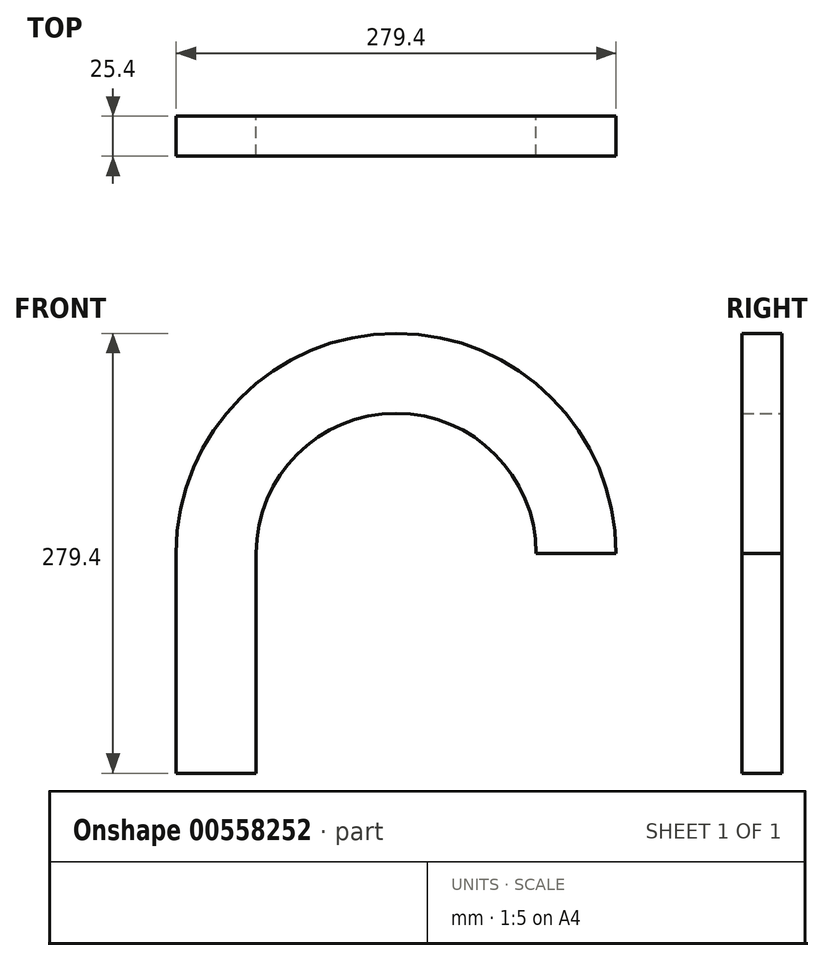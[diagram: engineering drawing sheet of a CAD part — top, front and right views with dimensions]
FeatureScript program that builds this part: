
annotation { "Feature Type Name" : "Feature", "Feature Type Description" : "" }
export const myFeature = defineFeature(function(context is Context, id is Id, definition is map)
    precondition{}
    {
        {
            var Q0;
            Q0=qCreatedBy(makeId("Front.planeOp"),FACE);
            var sketch = newSketch(context, id + "F0", { "sketchPlane" : qUnion([Q0])});
            skArc(sketch, "E0", {"start": v(139.7, 0) * mm, "mid": v(0, 139.7) * mm, "end": v(-139.7, 0) * mm});
            skArc(sketch, "E1", {"start": v(88.9, 0) * mm, "mid": v(0, 88.9) * mm, "end": v(-88.9, 0) * mm});
            skLineSegment(sketch, "E2", {"start": v(139.7, 0) * mm, "end": v(88.9, 0) * mm});
            skLineSegment(sketch, "E3", {"start": v(-139.7, 0) * mm, "end": v(-139.7, -139.7) * mm});
            skLineSegment(sketch, "E4", {"start": v(-139.7, -139.7) * mm, "end": v(-88.9, -139.7) * mm});
            skLineSegment(sketch, "E5", {"start": v(-88.9, -139.7) * mm, "end": v(-88.9, 0) * mm});
            skSolve(sketch);
        }
        {
            var Q0;
            Q0 = qSketchRegion(id + "F0", true);
            extrude(context, id + "F1", {"entities" : qUnion([Q0]), "depth" : 25.4 * mm, "offsetDistance" : 25.4 * mm});
        }
    });
